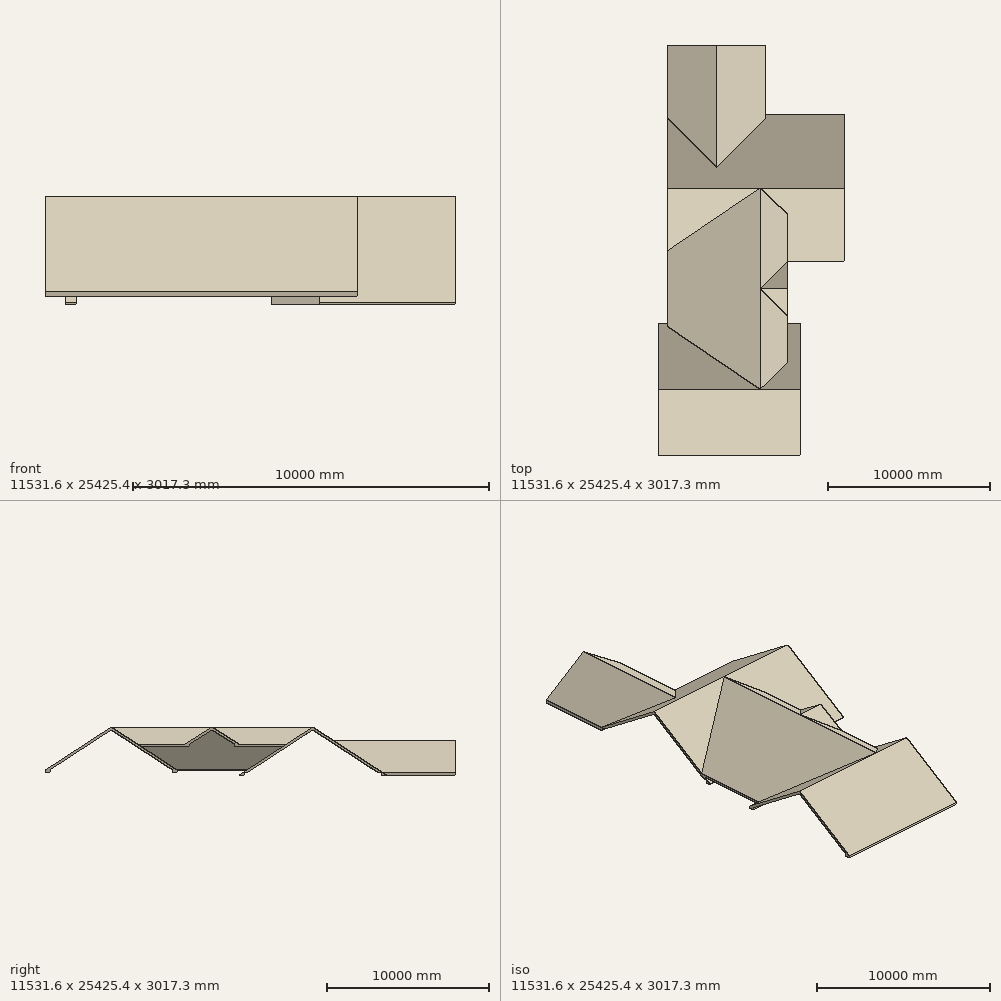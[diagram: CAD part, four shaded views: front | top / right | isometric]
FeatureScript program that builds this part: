
annotation { "Feature Type Name" : "Feature", "Feature Type Description" : "" }
export const myFeature = defineFeature(function(context is Context, id is Id, definition is map)
    precondition{}
    {
        {
            var Q0;
            Q0=qCreatedBy(makeId("Top.planeOp"),FACE);
            var sketch = newSketch(context, id + "F0", { "sketchPlane" : qUnion([Q0])});
            skLineSegment(sketch, "E0", {"start": v(0, 4267.2) * mm, "end": v(0, -4267.2) * mm, "construction": true});
            skLineSegment(sketch, "E1", {"start": v(0, 0) * mm, "end": v(-10363.2, 0) * mm, "construction": true});
            skLineSegment(sketch, "E2", {"start": v(0, 4267.2) * mm, "end": v(-4876.8, 4267.2) * mm, "construction": true});
            skLineSegment(sketch, "E3", {"start": v(-4876.8, 4267.2) * mm, "end": v(-4876.8, 8534.4) * mm, "construction": true});
            skLineSegment(sketch, "E4", {"start": v(-4876.8, 8534.4) * mm, "end": v(-10363.2, 8534.4) * mm, "construction": true});
            skLineSegment(sketch, "E5", {"start": v(-10363.2, 8534.4) * mm, "end": v(-10363.2, -8712.2) * mm, "construction": true});
            skLineSegment(sketch, "E6", {"start": v(-10363.2, -8712.2) * mm, "end": v(-10922, -8712.2) * mm, "construction": true});
            skLineSegment(sketch, "E7", {"start": v(-10922, -8712.2) * mm, "end": v(-10922, -16281.4) * mm, "construction": true});
            skLineSegment(sketch, "E8", {"start": v(-10922, -16281.4) * mm, "end": v(-2743.2, -16281.4) * mm, "construction": true});
            skLineSegment(sketch, "E9", {"start": v(-2743.2, -16281.4) * mm, "end": v(-2743.2, -8712.2) * mm, "construction": true});
            skLineSegment(sketch, "E10", {"start": v(-2743.2, -8712.2) * mm, "end": v(-3530.6, -8712.2) * mm, "construction": true});
            skLineSegment(sketch, "E11", {"start": v(-3530.6, -8712.2) * mm, "end": v(-3530.6, -4267.2) * mm, "construction": true});
            skLineSegment(sketch, "E12", {"start": v(-3530.6, -4267.2) * mm, "end": v(0, -4267.2) * mm, "construction": true});
            skLineSegment(sketch, "E13", {"start": v(-10922, -12496.8) * mm, "end": v(-2743.2, -12496.8) * mm, "construction": true});
            skLineSegment(sketch, "E14", {"start": v(-7620, 8534.4) * mm, "end": v(-7620, 0) * mm, "construction": true});
            skLineSegment(sketch, "E15", {"start": v(-4911.73, 0) * mm, "end": v(-4911.72, -12496.8) * mm, "construction": true});
            skLineSegment(sketch, "E16", {"start": v(-3530.6, -6489.7) * mm, "end": v(-4911.73, -6489.7) * mm, "construction": true});
            skSolve(sketch);
        }
        {
            var Q0;
            Q0=qCreatedBy(makeId("Right.planeOp"),FACE);
            cPlane(context, id + "F1", {"entities" : qUnion([Q0]), "cplaneType" : CPlaneType.OFFSET, "offset" : 2743.2 * mm, "oppositeDirection" : true, "width" : 152.4 * mm, "height" : 152.4 * mm});
        }
        {
            var Q0;
            Q0=qCreatedBy(makeId("Front.planeOp"),FACE);
            cPlane(context, id + "F2", {"entities" : qUnion([Q0]), "cplaneType" : CPlaneType.OFFSET, "offset" : 6489.7 * mm, "width" : 152.4 * mm, "height" : 152.4 * mm});
        }
        {
            var Q0;
            Q0=qCreatedBy(makeId("Front.planeOp"),FACE);
            cPlane(context, id + "F3", {"entities" : qUnion([Q0]), "cplaneType" : CPlaneType.OFFSET, "offset" : 8534.4 * mm, "oppositeDirection" : true, "width" : 152.4 * mm, "height" : 152.4 * mm});
        }
        {
            var Q0;
            Q0=qCreatedBy(makeId("Right.planeOp"),FACE);
            var sketch = newSketch(context, id + "F4", { "sketchPlane" : qUnion([Q0])});
            skLineSegment(sketch, "E17", {"start": v(0, 0) * mm, "end": v(0, -2632.08) * mm, "construction": true});
            skPoint(sketch, "E18", {"position": v(0, -2413) * mm});
            skLineSegment(sketch, "E19", {"start": v(-1828.8, -2413) * mm, "end": v(1828.8, -2413) * mm, "construction": true});
            skLineSegment(sketch, "E20", {"start": v(-1828.8, -2413) * mm, "end": v(-1828.8, -1193.8) * mm, "construction": true});
            skLineSegment(sketch, "E21", {"start": v(0, 0) * mm, "end": v(-4032.11, -2632.08) * mm});
            skLineSegment(sketch, "E22", {"start": v(-4267.2, -2632.08) * mm, "end": v(4267.2, -2632.08) * mm, "construction": true});
            skLineSegment(sketch, "E23", {"start": v(0, 182) * mm, "end": v(-4572, -2802.5) * mm});
            skLineSegment(sketch, "E24", {"start": v(-4267.2, -2835.28) * mm, "end": v(-4572, -2835.28) * mm});
            skLineSegment(sketch, "E25", {"start": v(-4572, -2835.28) * mm, "end": v(-4572, -2802.5) * mm});
            skLineSegment(sketch, "E26", {"start": v(-4032.11, -2632.08) * mm, "end": v(-4267.2, -2632.08) * mm});
            skLineSegment(sketch, "E27", {"start": v(-4267.2, -2835.28) * mm, "end": v(-4267.2, -2632.08) * mm});
            skLineSegment(sketch, "E28.MirrorCS", {"start": v(0, 0) * mm, "end": v(4032.11, -2632.08) * mm});
            skLineSegment(sketch, "E29.MirrorCS", {"start": v(0, 182) * mm, "end": v(4572, -2802.5) * mm});
            skLineSegment(sketch, "E30.MirrorCS", {"start": v(4572, -2835.28) * mm, "end": v(4572, -2802.5) * mm});
            skLineSegment(sketch, "E31.MirrorCS", {"start": v(4267.2, -2835.28) * mm, "end": v(4572, -2835.28) * mm});
            skLineSegment(sketch, "E32.MirrorCS", {"start": v(4267.2, -2835.28) * mm, "end": v(4267.2, -2632.08) * mm});
            skLineSegment(sketch, "E33.MirrorCS", {"start": v(4032.11, -2632.08) * mm, "end": v(4267.2, -2632.08) * mm});
            skSolve(sketch);
        }
        {
            var Q0;
            Q0 = qSketchRegion(id + "F4", true);
            extrude(context, id + "F5", {"entities" : qUnion([Q0]), "oppositeDirection" : true, "depth" : 10668 * mm, "hasSecondDirection" : true, "secondDirectionOppositeDirection" : false, "secondDirectionDepth" : 304.8 * mm});
        }
        {
            var Q0;
            Q0=qCreatedBy(id+"F1.planeOp",FACE);
            var sketch = newSketch(context, id + "F6", { "sketchPlane" : qUnion([Q0])});
            skLineSegment(sketch, "E34", {"start": v(-12496.8, 0) * mm, "end": v(-12496.8, -2632.08) * mm, "construction": true});
            skPoint(sketch, "E35", {"position": v(-12496.8, -2413) * mm});
            skLineSegment(sketch, "E36", {"start": v(-16281.4, -2632.08) * mm, "end": v(-8712.2, -2632.08) * mm, "construction": true});
            skLineSegment(sketch, "E37", {"start": v(-14325.6, -2413) * mm, "end": v(-10668, -2413) * mm, "construction": true});
            skLineSegment(sketch, "E38", {"start": v(-14325.6, -2413) * mm, "end": v(-14325.6, -1193.8) * mm, "construction": true});
            skLineSegment(sketch, "E39", {"start": v(-12496.8, 0) * mm, "end": v(-16281.4, -2470.5) * mm});
            skLineSegment(sketch, "E40", {"start": v(-12496.8, 182) * mm, "end": v(-16586.2, -2487.47) * mm});
            skLineSegment(sketch, "E41", {"start": v(-16281.4, -2470.5) * mm, "end": v(-16281.4, -2632.08) * mm});
            skLineSegment(sketch, "E42", {"start": v(-16281.4, -2632.08) * mm, "end": v(-16586.2, -2632.08) * mm});
            skLineSegment(sketch, "E43", {"start": v(-16586.2, -2632.08) * mm, "end": v(-16586.2, -2487.47) * mm});
            skLineSegment(sketch, "E44.MirrorCS", {"start": v(-12496.8, 0) * mm, "end": v(-8712.2, -2470.5) * mm});
            skLineSegment(sketch, "E45.MirrorCS", {"start": v(-12496.8, 182) * mm, "end": v(-8407.4, -2487.47) * mm});
            skLineSegment(sketch, "E46.MirrorCS", {"start": v(-8407.4, -2632.07) * mm, "end": v(-8407.4, -2487.47) * mm});
            skLineSegment(sketch, "E47.MirrorCS", {"start": v(-8712.2, -2632.07) * mm, "end": v(-8407.4, -2632.07) * mm});
            skLineSegment(sketch, "E48.MirrorCS", {"start": v(-8712.2, -2470.5) * mm, "end": v(-8712.2, -2632.07) * mm});
            skSolve(sketch);
        }
        {
            var Q0;
            Q0 = qSketchRegion(id + "F6", true);
            extrude(context, id + "F7", {"entities" : qUnion([Q0]), "oppositeDirection" : true, "depth" : 8483.6 * mm, "hasSecondDirection" : true, "secondDirectionOppositeDirection" : false, "secondDirectionDepth" : 304.8 * mm});
        }
        {
            var Q0;
            Q0=qCreatedBy(id+"F2.planeOp",FACE);
            var sketch = newSketch(context, id + "F8", { "sketchPlane" : qUnion([Q0])});
            skLineSegment(sketch, "E49", {"start": v(-4911.73, 0) * mm, "end": v(-4911.73, -2632.08) * mm, "construction": true});
            skPoint(sketch, "E50", {"position": v(-4911.73, -2413) * mm});
            skLineSegment(sketch, "E51", {"start": v(-4911.73, -2413) * mm, "end": v(-3657.6, -2413) * mm, "construction": true});
            skLineSegment(sketch, "E52", {"start": v(-3657.6, -2413) * mm, "end": v(-3657.6, -787.4) * mm, "construction": true});
            skLineSegment(sketch, "E53", {"start": v(-4911.73, 0) * mm, "end": v(-3530.6, -867.14) * mm});
            skLineSegment(sketch, "E54", {"start": v(-4911.73, 179.95) * mm, "end": v(-3225.8, -878.56) * mm});
            skLineSegment(sketch, "E55", {"start": v(-3530.6, -867.14) * mm, "end": v(-3530.6, -1005.56) * mm});
            skLineSegment(sketch, "E56", {"start": v(-3530.6, -1005.56) * mm, "end": v(-3225.8, -1005.56) * mm});
            skLineSegment(sketch, "E57", {"start": v(-3225.8, -878.56) * mm, "end": v(-3225.8, -1005.56) * mm});
            skLineSegment(sketch, "E58", {"start": v(-4911.73, 0) * mm, "end": v(-10363.2, -2413) * mm});
            skLineSegment(sketch, "E59", {"start": v(-4911.73, -2413) * mm, "end": v(-10363.2, -2413) * mm, "construction": true});
            skLineSegment(sketch, "E60", {"start": v(-10363.2, -2413) * mm, "end": v(-10363.2, -2520.37) * mm});
            skLineSegment(sketch, "E61", {"start": v(-10363.2, -2520.37) * mm, "end": v(-10668, -2520.37) * mm});
            skLineSegment(sketch, "E62", {"start": v(-4911.73, 179.95) * mm, "end": v(-10668, -2367.97) * mm});
            skLineSegment(sketch, "E63", {"start": v(-10668, -2520.37) * mm, "end": v(-10668, -2367.97) * mm});
            skSolve(sketch);
        }
        {
            var Q0;
            Q0 = qSketchRegion(id + "F8", true);
            extrude(context, id + "F9", {"entities" : qUnion([Q0]), "operationType" : NewBodyOperationType.ADD, "endBound" : BoundingType.UP_TO_NEXT, "oppositeDirection" : true, "depth" : 25.4 * mm, "hasSecondDirection" : true, "secondDirectionBound" : BoundingType.UP_TO_NEXT, "secondDirectionOppositeDirection" : false, "secondDirectionDepth" : 25.4 * mm});
        }
        {
            var Q0;
            Q0=qCreatedBy(id+"F2.planeOp",FACE);
            var sketch = newSketch(context, id + "F10", { "sketchPlane" : qUnion([Q0])});
            skLineSegment(sketch, "E64", {"start": v(-4911.72, 0) * mm, "end": v(-10363.2, -2413) * mm});
            skLineSegment(sketch, "E65", {"start": v(-10363.2, -2413) * mm, "end": v(-10363.2, -2835.28) * mm});
            skLineSegment(sketch, "E66", {"start": v(-10363.2, -2835.28) * mm, "end": v(-3530.6, -2835.28) * mm});
            skLineSegment(sketch, "E67", {"start": v(-3530.6, -2835.28) * mm, "end": v(-3530.6, -867.14) * mm});
            skLineSegment(sketch, "E68", {"start": v(-3530.6, -867.14) * mm, "end": v(-4911.72, 0) * mm});
            skSolve(sketch);
        }
        {
            var Q0;
            Q0 = qSketchRegion(id + "F10", true);
            var Q1;
            Q1=qCreatedBy(makeId("Front.planeOp"),FACE);
            extrude(context, id + "F11", {"entities" : qUnion([Q0]), "operationType" : NewBodyOperationType.REMOVE, "endBound" : BoundingType.UP_TO_SURFACE, "oppositeDirection" : true, "endBoundEntityFace" : qUnion([Q1]), "depth" : 25.4 * mm, "hasSecondDirection" : true, "secondDirectionOppositeDirection" : false, "secondDirectionDepth" : 6019.8 * mm});
        }
        {
            var Q0;
            Q0=qCreatedBy(id+"F3.planeOp",FACE);
            var sketch = newSketch(context, id + "F12", { "sketchPlane" : qUnion([Q0])});
            skLineSegment(sketch, "E69", {"start": v(-7620, 0) * mm, "end": v(-7620, -2632.08) * mm, "construction": true});
            skPoint(sketch, "E70", {"position": v(-7620, -2413) * mm});
            skPoint(sketch, "E71", {"position": v(-7620, -838.2) * mm});
            skLineSegment(sketch, "E72", {"start": v(-5791.2, -2413) * mm, "end": v(-9448.8, -2413) * mm, "construction": true});
            skLineSegment(sketch, "E73", {"start": v(-5791.2, -2413) * mm, "end": v(-5791.2, -2032) * mm, "construction": true});
            skLineSegment(sketch, "E74", {"start": v(-4876.8, -2632.08) * mm, "end": v(-10363.2, -2632.08) * mm, "construction": true});
            skLineSegment(sketch, "E75", {"start": v(-7620, -838.2) * mm, "end": v(-4876.8, -2628.9) * mm});
            skLineSegment(sketch, "E76", {"start": v(-4876.8, -2628.9) * mm, "end": v(-4876.8, -2832.1) * mm});
            skLineSegment(sketch, "E77", {"start": v(-4876.8, -2832.1) * mm, "end": v(-4572, -2832.1) * mm});
            skLineSegment(sketch, "E78", {"start": v(-7620, -656.2) * mm, "end": v(-4572, -2645.87) * mm});
            skLineSegment(sketch, "E79", {"start": v(-4572, -2832.1) * mm, "end": v(-4572, -2645.87) * mm});
            skLineSegment(sketch, "E80.MirrorCS", {"start": v(-7620, -838.2) * mm, "end": v(-10363.2, -2628.9) * mm});
            skLineSegment(sketch, "E81.MirrorCS", {"start": v(-10363.2, -2628.9) * mm, "end": v(-10363.2, -2832.1) * mm});
            skLineSegment(sketch, "E82.MirrorCS", {"start": v(-10363.2, -2832.1) * mm, "end": v(-10668, -2832.1) * mm});
            skLineSegment(sketch, "E83.MirrorCS", {"start": v(-10668, -2832.1) * mm, "end": v(-10668, -2645.87) * mm});
            skLineSegment(sketch, "E84.MirrorCS", {"start": v(-7620, -656.2) * mm, "end": v(-10668, -2645.87) * mm});
            skSolve(sketch);
        }
        {
            var Q0;
            Q0 = qSketchRegion(id + "F12", true);
            extrude(context, id + "F13", {"entities" : qUnion([Q0]), "operationType" : NewBodyOperationType.ADD, "endBound" : BoundingType.UP_TO_NEXT, "depth" : 25.4 * mm, "hasSecondDirection" : true, "secondDirectionOppositeDirection" : true, "secondDirectionDepth" : 304.8 * mm});
        }
        {
            var Q0;
            Q0=makeQuery(id+"F13.opExtrude","CAP_FACE",FACE,{"disambiguationData":[OSD([sQuery(id+"F12.wireOp",EDGE,"E75"),sQuery(id+"F12.wireOp",EDGE,"E76"),sQuery(id+"F12.wireOp",EDGE,"E77"),sQuery(id+"F12.wireOp",EDGE,"E78"),sQuery(id+"F12.wireOp",EDGE,"E79"),sQuery(id+"F12.wireOp",EDGE,"E80.MirrorCS"),sQuery(id+"F12.wireOp",EDGE,"E81.MirrorCS"),sQuery(id+"F12.wireOp",EDGE,"E82.MirrorCS"),sQuery(id+"F12.wireOp",EDGE,"E83.MirrorCS"),sQuery(id+"F12.wireOp",EDGE,"E84.MirrorCS")])],"isStart":true});
            var sketch = newSketch(context, id + "F14", { "sketchPlane" : qUnion([Q0])});
            skLineSegment(sketch, "E85", {"start": v(7620, -838.2) * mm, "end": v(4876.8, -2628.9) * mm});
            skLineSegment(sketch, "E86", {"start": v(4876.8, -2628.9) * mm, "end": v(4876.8, -2835.28) * mm});
            skLineSegment(sketch, "E87", {"start": v(4876.8, -2835.28) * mm, "end": v(10363.2, -2835.28) * mm});
            skLineSegment(sketch, "E88", {"start": v(10363.2, -2835.28) * mm, "end": v(10363.2, -2628.9) * mm});
            skLineSegment(sketch, "E89", {"start": v(10363.2, -2628.9) * mm, "end": v(7620, -838.2) * mm});
            skSolve(sketch);
        }
        {
            var Q0;
            Q0 = qSketchRegion(id + "F14", true);
            var Q1;
            Q1=qCreatedBy(makeId("Front.planeOp"),FACE);
            extrude(context, id + "F15", {"entities" : qUnion([Q0]), "operationType" : NewBodyOperationType.REMOVE, "endBound" : BoundingType.UP_TO_SURFACE, "oppositeDirection" : true, "endBoundEntityFace" : qUnion([Q1]), "depth" : 25.4 * mm});
        }
        {
            var Q0;
            Q0=makeQuery(id+"F9.opExtrude","SWEPT_FACE",FACE,{"disambiguationData":[OSD([sQuery(id+"F8.wireOp",EDGE,"E57")])]});
            var sketch = newSketch(context, id + "F16", { "sketchPlane" : qUnion([Q0])});
            skLineSegment(sketch, "E90", {"start": v(-6248.4, 0) * mm, "end": v(-6248.4, -2632.08) * mm, "construction": true});
            skPoint(sketch, "E91", {"position": v(-6248.4, -2413) * mm});
            skLineSegment(sketch, "E92", {"start": v(-7502.53, -2413) * mm, "end": v(-4994.27, -2413) * mm, "construction": true});
            skLineSegment(sketch, "E93", {"start": v(-7502.53, -2413) * mm, "end": v(-7502.53, -787.4) * mm, "construction": true});
            skLineSegment(sketch, "E94", {"start": v(-6248.4, 0) * mm, "end": v(-7647.71, -878.56) * mm});
            skLineSegment(sketch, "E95", {"start": v(-6248.4, 179.95) * mm, "end": v(-7934.33, -878.56) * mm});
            skLineSegment(sketch, "E96", {"start": v(-7647.71, -878.56) * mm, "end": v(-7934.33, -878.56) * mm});
            skLineSegment(sketch, "E97.MirrorCS", {"start": v(-6248.4, 0) * mm, "end": v(-4849.09, -878.56) * mm});
            skLineSegment(sketch, "E98.MirrorCS", {"start": v(-4849.09, -878.56) * mm, "end": v(-4562.47, -878.56) * mm});
            skLineSegment(sketch, "E99.MirrorCS", {"start": v(-6248.4, 179.95) * mm, "end": v(-4562.47, -878.56) * mm});
            skLineSegment(sketch, "E100", {"start": v(-12496.8, 0) * mm, "end": v(0, 0) * mm, "construction": true});
            skSolve(sketch);
        }
        {
            var Q0;
            Q0 = qSketchRegion(id + "F16", true);
            extrude(context, id + "F17", {"entities" : qUnion([Q0]), "operationType" : NewBodyOperationType.ADD, "endBound" : BoundingType.UP_TO_NEXT, "oppositeDirection" : true, "depth" : 25.4 * mm});
        }
        {
            var Q0;
            Q0=makeQuery(id+"F17.boolean.opBoolean","MERGE",FACE,{"derivedFrom":[makeQuery(id+"F9.opExtrude","SWEPT_FACE",FACE,{"disambiguationData":[OSD([sQuery(id+"F8.wireOp",EDGE,"E57")])]}),makeQuery(id+"F17.opExtrude","CAP_FACE",FACE,{"disambiguationData":[OSD([sQuery(id+"F16.wireOp",EDGE,"E94"),sQuery(id+"F16.wireOp",EDGE,"E95"),sQuery(id+"F16.wireOp",EDGE,"E96"),sQuery(id+"F16.wireOp",EDGE,"E97.MirrorCS"),sQuery(id+"F16.wireOp",EDGE,"E98.MirrorCS"),sQuery(id+"F16.wireOp",EDGE,"E99.MirrorCS")])],"isStart":true})]});
            var sketch = newSketch(context, id + "F18", { "sketchPlane" : qUnion([Q0])});
            skLineSegment(sketch, "E101", {"start": v(-6248.4, 0) * mm, "end": v(-7647.71, -878.56) * mm});
            skLineSegment(sketch, "E102", {"start": v(-7647.71, -878.56) * mm, "end": v(-7647.71, -1005.56) * mm});
            skLineSegment(sketch, "E103", {"start": v(-7647.71, -1005.56) * mm, "end": v(-4849.09, -1005.56) * mm});
            skLineSegment(sketch, "E104", {"start": v(-4849.09, -1005.56) * mm, "end": v(-4849.09, -878.56) * mm});
            skLineSegment(sketch, "E105", {"start": v(-4849.09, -878.56) * mm, "end": v(-6248.4, 0) * mm});
            skSolve(sketch);
        }
        {
            var Q0;
            Q0 = qSketchRegion(id + "F18", true);
            extrude(context, id + "F19", {"entities" : qUnion([Q0]), "operationType" : NewBodyOperationType.REMOVE, "oppositeDirection" : true, "depth" : 1685.92 * mm});
        }
    });
